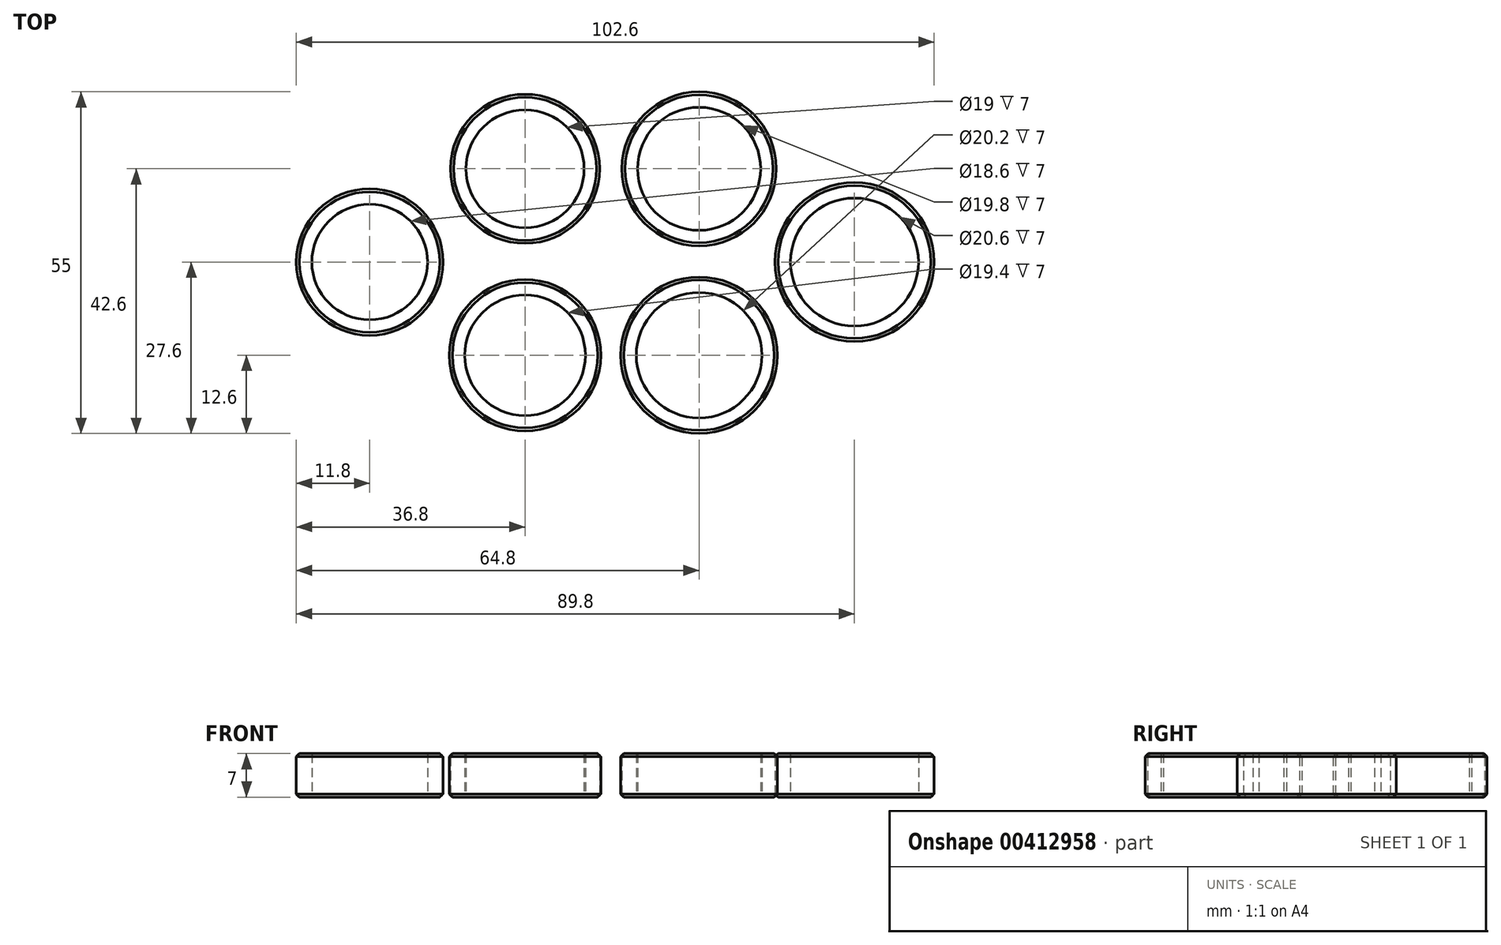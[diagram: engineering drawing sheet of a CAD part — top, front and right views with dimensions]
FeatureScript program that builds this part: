
annotation { "Feature Type Name" : "Feature", "Feature Type Description" : "" }
export const myFeature = defineFeature(function(context is Context, id is Id, definition is map)
    precondition{}
    {
        {
            var Q0;
            Q0=qCreatedBy(makeId("Top.planeOp"),FACE);
            var sketch = newSketch(context, id + "F0", { "sketchPlane" : qUnion([Q0])});
            skCircle(sketch, "E0", {"center": v(0, 0) * mm, "radius": 9.9 * mm});
            skCircle(sketch, "E1.0", {"center": v(0, 0) * mm, "radius": 12.4 * mm});
            skCircle(sketch, "E2", {"center": v(0, -30) * mm, "radius": 10.1 * mm});
            skCircle(sketch, "E3.0", {"center": v(0, -30) * mm, "radius": 12.6 * mm});
            skCircle(sketch, "E4", {"center": v(-28, -30) * mm, "radius": 9.7 * mm});
            skCircle(sketch, "E5.0", {"center": v(-28, -30) * mm, "radius": 12.2 * mm});
            skCircle(sketch, "E6", {"center": v(-28, 0) * mm, "radius": 9.5 * mm});
            skCircle(sketch, "E7.0", {"center": v(-28, 0) * mm, "radius": 12 * mm});
            skCircle(sketch, "E8", {"center": v(25, -15) * mm, "radius": 10.3 * mm});
            skCircle(sketch, "E9.0", {"center": v(25, -15) * mm, "radius": 12.8 * mm});
            skCircle(sketch, "E10", {"center": v(-53, -15) * mm, "radius": 9.3 * mm});
            skCircle(sketch, "E11.0", {"center": v(-53, -15) * mm, "radius": 11.8 * mm});
            skSolve(sketch);
        }
        {
            var Q0;
            Q0=makeQuery(id+"F0.imprint","IMPRINT",FACE,{"disambiguationData":[TD([[makeQuery(id+"F0.imprint","IMPRINT",EDGE,{"derivedFrom":sQuery(id+"F0.wireOp",EDGE,"E10")}),-1.0]])]});
            var Q1;
            Q1=makeQuery(id+"F0.imprint","IMPRINT",FACE,{"disambiguationData":[TD([[makeQuery(id+"F0.imprint","IMPRINT",EDGE,{"derivedFrom":sQuery(id+"F0.wireOp",EDGE,"E6")}),-1.0]])]});
            var Q2;
            Q2=makeQuery(id+"F0.imprint","IMPRINT",FACE,{"disambiguationData":[TD([[makeQuery(id+"F0.imprint","IMPRINT",EDGE,{"derivedFrom":sQuery(id+"F0.wireOp",EDGE,"E0")}),-1.0]])]});
            var Q3;
            Q3=makeQuery(id+"F0.imprint","IMPRINT",FACE,{"disambiguationData":[TD([[makeQuery(id+"F0.imprint","IMPRINT",EDGE,{"derivedFrom":sQuery(id+"F0.wireOp",EDGE,"E8")}),-1.0]])]});
            var Q4;
            Q4=makeQuery(id+"F0.imprint","IMPRINT",FACE,{"disambiguationData":[TD([[makeQuery(id+"F0.imprint","IMPRINT",EDGE,{"derivedFrom":sQuery(id+"F0.wireOp",EDGE,"E2")}),-1.0]])]});
            var Q5;
            Q5=makeQuery(id+"F0.imprint","IMPRINT",FACE,{"disambiguationData":[TD([[makeQuery(id+"F0.imprint","IMPRINT",EDGE,{"derivedFrom":sQuery(id+"F0.wireOp",EDGE,"E4")}),-1.0]])]});
            extrude(context, id + "F1", {"entities" : qUnion([Q0, Q1, Q2, Q3, Q4, Q5]), "depth" : 7 * mm});
        }
        {
            var Q0;
            Q0=makeQuery(id+"F1.opExtrude","CAP_EDGE",EDGE,{"disambiguationData":[OSD([sQuery(id+"F0.wireOp",EDGE,"E11.0")])],"isStart":false});
            var Q1;
            Q1=makeQuery(id+"F1.opExtrude","CAP_EDGE",EDGE,{"disambiguationData":[OSD([sQuery(id+"F0.wireOp",EDGE,"E11.0")])],"isStart":true});
            var Q2;
            Q2=makeQuery(id+"F1.opExtrude","CAP_EDGE",EDGE,{"disambiguationData":[OSD([sQuery(id+"F0.wireOp",EDGE,"E7.0")])],"isStart":false});
            var Q3;
            Q3=makeQuery(id+"F1.opExtrude","CAP_EDGE",EDGE,{"disambiguationData":[OSD([sQuery(id+"F0.wireOp",EDGE,"E7.0")])],"isStart":true});
            var Q4;
            Q4=makeQuery(id+"F1.opExtrude","CAP_EDGE",EDGE,{"disambiguationData":[OSD([sQuery(id+"F0.wireOp",EDGE,"E1.0")])],"isStart":true});
            var Q5;
            Q5=makeQuery(id+"F1.opExtrude","CAP_EDGE",EDGE,{"disambiguationData":[OSD([sQuery(id+"F0.wireOp",EDGE,"E1.0")])],"isStart":false});
            var Q6;
            Q6=makeQuery(id+"F1.opExtrude","CAP_EDGE",EDGE,{"disambiguationData":[OSD([sQuery(id+"F0.wireOp",EDGE,"E9.0")])],"isStart":false});
            var Q7;
            Q7=makeQuery(id+"F1.opExtrude","CAP_EDGE",EDGE,{"disambiguationData":[OSD([sQuery(id+"F0.wireOp",EDGE,"E9.0")])],"isStart":true});
            var Q8;
            Q8=makeQuery(id+"F1.opExtrude","CAP_EDGE",EDGE,{"disambiguationData":[OSD([sQuery(id+"F0.wireOp",EDGE,"E3.0")])],"isStart":false});
            var Q9;
            Q9=makeQuery(id+"F1.opExtrude","CAP_EDGE",EDGE,{"disambiguationData":[OSD([sQuery(id+"F0.wireOp",EDGE,"E3.0")])],"isStart":true});
            var Q10;
            Q10=makeQuery(id+"F1.opExtrude","CAP_EDGE",EDGE,{"disambiguationData":[OSD([sQuery(id+"F0.wireOp",EDGE,"E5.0")])],"isStart":false});
            var Q11;
            Q11=makeQuery(id+"F1.opExtrude","CAP_EDGE",EDGE,{"disambiguationData":[OSD([sQuery(id+"F0.wireOp",EDGE,"E5.0")])],"isStart":true});
            chamfer(context, id + "F2", {"entities" : qUnion([Q0, Q1, Q2, Q3, Q4, Q5, Q6, Q7, Q8, Q9, Q10, Q11]), "width" : 0.5 * mm, "tangentPropagation" : true});
        }
    });
